# Revit family: VENTS-VKP_EC
name_source: partatom
category: Mechanical Equipment
units: mm (PartAtom-declared; Revit-internal decimal feet)

## family parameters
Always vertical = Yes
Classification = None
Cut with Voids When Loaded = No
OmniClass Number = 23.75.35.17.11
OmniClass Title = Fans for Air Ductwork
Part Type = Breaks Into
Room Calculation Point = No
Round Connector Dimension = Use Diameter
Shared = No
Work Plane-Based = No

## types (16) — shared parameters
Casing Material = Fan Zinc
Description = Inline centrifugal fan for rectangular ducts
Distribution Box Material = Distribution Box
Family Version = 1.0
Load Classification = HVAC
Maintenance Zone Height = 600 mm
Maintenance Zone Material = Maintenance Zone
Manufacturer = Vents
Motor Material = Painted Steel Black
Power Factor = 1
Protection rating = IP X4
Transported Air Temperature (°C) = -25...+40
URL = https://ventilation-system.com
dFl = 20 mm  [stored 0.0656168 ft]

## per-type parameters (varying)
- VKP 300x150 M1 EC: Apparent Power=97 VA; B=300 mm; B2=340 mm; Connection H=150 mm; Connection W=300 mm; Current=1 A; H=150 mm; H2=190 mm; L=350 mm; Maintenance Zone Length=350 mm; Maintenance Zone Width=300 mm; Maximum Air Flow=565 m³/h; Motor=No; Noise Level at 3 m (dBa)=44; Number of Poles=1; Power=97 W; RPM (min-1)=3300; Type Comments=Inline centrifugal fan VKP 300x150 M1 EC; Voltage=230 V; Weight=5.50 kg; eL=150 mm; eW=85 mm  [stored 0.278871 ft]; gsD=150 mm; mD=96 mm  [stored 0.314961 ft]; mH1=1 mm  [stored 0.00328084 ft]; mH2=30 mm  [stored 0.0984252 ft]; mL=145 mm  [stored 0.475722 ft]; mLW=122 mm  [stored 0.400262 ft]; mW=127 mm
- VKP 300х150 L1 EC: Apparent Power=101 VA; B=300 mm; B2=340 mm; Connection H=150 mm; Connection W=300 mm; Current=1 A; H=150 mm; H2=190 mm; L=350 mm; Maintenance Zone Length=350 mm; Maintenance Zone Width=300 mm; Maximum Air Flow=665 m³/h; Motor=Yes; Noise Level at 3 m (dBa)=46; Number of Poles=1; Power=101 W; RPM (min-1)=3500; Type Comments=Inline centrifugal fan VKP 300х150 L1 EC; Voltage=230 V; Weight=6.00 kg; eL=145 mm  [stored 0.475722 ft]; eW=68 mm; gsD=150 mm; mD=96 mm  [stored 0.314961 ft]; mH1=1 mm  [stored 0.00328084 ft]; mH2=30 mm  [stored 0.0984252 ft]; mL=145 mm  [stored 0.475722 ft]; mLW=122 mm  [stored 0.400262 ft]; mW=127 mm
- VKP 400x200 M1 EC: Apparent Power=91 VA; B=400 mm; B2=440 mm; Connection H=200 mm  [stored 0.656168 ft]; Connection W=400 mm; Current=1 A; H=200 mm  [stored 0.656168 ft]; H2=240 mm  [stored 0.787402 ft]; L=440 mm; Maintenance Zone Length=440 mm; Maintenance Zone Width=400 mm; Maximum Air Flow=810 m³/h; Motor=No; Noise Level at 3 m (dBa)=43; Number of Poles=1; Power=91 W; RPM (min-1)=2470; Type Comments=Inline centrifugal fan VKP 400x200 M1 EC; Voltage=230 V; Weight=8.30 kg; eL=195 mm  [stored 0.639764 ft]; eW=148 mm  [stored 0.485564 ft]; gsD=200 mm  [stored 0.656168 ft]; mD=96 mm  [stored 0.314961 ft]; mH1=1 mm  [stored 0.00328084 ft]; mH2=30 mm  [stored 0.0984252 ft]; mL=145 mm  [stored 0.475722 ft]; mLW=122 mm  [stored 0.400262 ft]; mW=127 mm
- VKP 400x200 L1 EC: Apparent Power=192 VA; B=400 mm; B2=440 mm; Connection H=200 mm  [stored 0.656168 ft]; Connection W=400 mm; Current=1 A; H=200 mm  [stored 0.656168 ft]; H2=240 mm  [stored 0.787402 ft]; L=440 mm; Maintenance Zone Length=440 mm; Maintenance Zone Width=400 mm; Maximum Air Flow=1190 m³/h; Motor=Yes; Noise Level at 3 m (dBa)=47; Number of Poles=1; Power=192 W; RPM (min-1)=3010; Type Comments=Inline centrifugal fan VKP 400x200 L1 EC; Voltage=230 V; Weight=10.00 kg; eL=195 mm  [stored 0.639764 ft]; eW=117 mm  [stored 0.383858 ft]; gsD=200 mm  [stored 0.656168 ft]; mD=114 mm  [stored 0.374016 ft]; mH1=1 mm  [stored 0.00328084 ft]; mH2=40 mm  [stored 0.131234 ft]; mL=195 mm  [stored 0.639764 ft]; mLW=142 mm  [stored 0.465879 ft]; mW=167 mm  [stored 0.5479 ft]
- VKP 500x250 M1 EC: Apparent Power=252 VA; B=500 mm; B2=540 mm; Connection H=250 mm  [stored 0.82021 ft]; Connection W=500 mm; Current=2 A; H=250 mm  [stored 0.82021 ft]; H2=290 mm; L=530 mm; Maintenance Zone Length=530 mm; Maintenance Zone Width=500 mm; Maximum Air Flow=1590 m³/h; Motor=Yes; Noise Level at 3 m (dBa)=45; Number of Poles=1; Power=252 W; RPM (min-1)=2500; Type Comments=Inline centrifugal fan VKP 500x250 M1 EC; Voltage=230 V; Weight=15.70 kg; eL=208 mm; eW=122 mm  [stored 0.400262 ft]; gsD=250 mm  [stored 0.82021 ft]; mD=114 mm  [stored 0.374016 ft]; mH1=1 mm  [stored 0.00328084 ft]; mH2=42 mm  [stored 0.137795 ft]; mL=215 mm; mLW=142 mm  [stored 0.465879 ft]; mW=208 mm
- VKP 500x250 L1 EC: Apparent Power=555 VA; B=500 mm; B2=540 mm; Connection H=250 mm  [stored 0.82021 ft]; Connection W=500 mm; Current=4 A; H=250 mm  [stored 0.82021 ft]; H2=290 mm; L=530 mm; Maintenance Zone Length=530 mm; Maintenance Zone Width=500 mm; Maximum Air Flow=2480 m³/h; Motor=Yes; Noise Level at 3 m (dBa)=51; Number of Poles=1; Power=555 W; RPM (min-1)=3100; Type Comments=Inline centrifugal fan VKP 500x250 L1 EC; Voltage=230 V; Weight=17.90 kg; eL=208 mm; eW=117 mm  [stored 0.383858 ft]; gsD=250 mm  [stored 0.82021 ft]; mD=153 mm  [stored 0.501969 ft]; mH1=42 mm  [stored 0.137795 ft]; mH2=47 mm  [stored 0.154199 ft]; mL=215 mm; mLW=192 mm  [stored 0.629921 ft]; mW=208 mm
- VKP 500x300 L1 EC: Apparent Power=445 VA; B=500 mm; B2=540 mm; Connection H=300 mm; Connection W=500 mm; Current=3 A; H=300 mm; H2=340 mm; L=530 mm; Maintenance Zone Length=530 mm; Maintenance Zone Width=500 mm; Maximum Air Flow=3230 m³/h; Motor=Yes; Noise Level at 3 m (dBa)=51; Number of Poles=1; Power=445 W; RPM (min-1)=3100; Type Comments=Inline centrifugal fan VKP 500x300 L1 EC; Voltage=230 V; Weight=18.70 kg; eL=208 mm; eW=117 mm  [stored 0.383858 ft]; gsD=250 mm  [stored 0.82021 ft]; mD=153 mm  [stored 0.501969 ft]; mH1=42 mm  [stored 0.137795 ft]; mH2=47 mm  [stored 0.154199 ft]; mL=215 mm; mLW=192 mm  [stored 0.629921 ft]; mW=208 mm
- VKP 600x300 M1 EC: Apparent Power=326 VA; B=600 mm; B2=640 mm; Connection H=300 mm; Connection W=600 mm; Current=2 A; H=300 mm; H2=340 mm; L=650 mm; Maintenance Zone Length=650 mm; Maintenance Zone Width=600 mm; Maximum Air Flow=2545 m³/h; Motor=Yes; Noise Level at 3 m (dBa)=48; Number of Poles=1; Power=326 W; RPM (min-1)=2000; Type Comments=Inline centrifugal fan VKP 600x300 M1 EC; Voltage=230 V; Weight=24.10 kg; eL=342 mm; eW=178 mm  [stored 0.58399 ft]; gsD=300 mm; mD=153 mm  [stored 0.501969 ft]; mH1=39 mm  [stored 0.127953 ft]; mH2=47 mm  [stored 0.154199 ft]; mL=265 mm; mLW=192 mm  [stored 0.629921 ft]; mW=252 mm
- VKP 600x350 M1 EC: Apparent Power=361 VA; B=600 mm; B2=640 mm; Connection H=350 mm; Connection W=600 mm; Current=3 A; H=350 mm; H2=390 mm; L=650 mm; Maintenance Zone Length=650 mm; Maintenance Zone Width=600 mm; Maximum Air Flow=2815 m³/h; Motor=Yes; Noise Level at 3 m (dBa)=49; Number of Poles=1; Power=361 W; RPM (min-1)=2000; Type Comments=Inline centrifugal fan VKP 600x350 M1 EC; Voltage=230 V; Weight=25.20 kg; eL=342 mm; eW=178 mm  [stored 0.58399 ft]; gsD=300 mm; mD=153 mm  [stored 0.501969 ft]; mH1=39 mm  [stored 0.127953 ft]; mH2=47 mm  [stored 0.154199 ft]; mL=265 mm; mLW=192 mm  [stored 0.629921 ft]; mW=252 mm
- VKP 600x350 LЗ EC: Apparent Power=1308 VA; B=600 mm; B2=640 mm; Connection H=350 mm; Connection W=600 mm; Current=2 A; H=350 mm; H2=390 mm; L=650 mm; Maintenance Zone Length=650 mm; Maintenance Zone Width=600 mm; Maximum Air Flow=4290 m³/h; Motor=Yes; Noise Level at 3 m (dBa)=55; Number of Poles=3; Power=1308 W; RPM (min-1)=3160; Type Comments=Inline centrifugal fan VKP 600x350 LЗ EC; Voltage=400 V; Weight=36.00 kg; eL=342 mm; eW=117 mm  [stored 0.383858 ft]; gsD=300 mm; mD=230 mm  [stored 0.754593 ft]; mH1=65 mm  [stored 0.213255 ft]; mH2=75 mm; mL=265 mm; mLW=288 mm; mW=252 mm
- VKP 700x400 M1 EC: Apparent Power=795 VA; B=700 mm; B2=740 mm; Connection H=400 mm; Connection W=700 mm; Current=3 A; H=400 mm; H2=440 mm; L=750 mm; Maintenance Zone Length=750 mm; Maintenance Zone Width=700 mm; Maximum Air Flow=5710 m³/h; Motor=Yes; Noise Level at 3 m (dBa)=53; Number of Poles=1; Power=795 W; RPM (min-1)=1400; Type Comments=Inline centrifugal fan VKP 700x400 M1 EC; Voltage=230 V; Weight=42.20 kg; eL=315 mm; eW=188 mm  [stored 0.616798 ft]; gsD=350 mm; mD=171 mm  [stored 0.561024 ft]; mH1=15 mm  [stored 0.0492126 ft]; mH2=60 mm  [stored 0.19685 ft]; mL=330 mm; mLW=288 mm; mW=292 mm
- VKP 700x400 LЗ EC: Apparent Power=2748 VA; B=700 mm; B2=740 mm; Connection H=400 mm; Connection W=700 mm; Current=3 A; H=400 mm; H2=440 mm; L=750 mm; Maintenance Zone Length=750 mm; Maintenance Zone Width=700 mm; Maximum Air Flow=6810 m³/h; Motor=Yes; Noise Level at 3 m (dBa)=57; Number of Poles=3; Power=2748 W; RPM (min-1)=2530; Type Comments=Inline centrifugal fan VKP 700x400 LЗ EC; Voltage=400 V; Weight=43.00 kg; eL=315 mm; eW=188 mm  [stored 0.616798 ft]; gsD=350 mm; mD=230 mm  [stored 0.754593 ft]; mH1=60 mm  [stored 0.19685 ft]; mH2=74 mm  [stored 0.242782 ft]; mL=330 mm; mLW=288 mm; mW=292 mm
- VKP 800x500 MЗ EC: Apparent Power=2025 VA; B=800 mm; B2=840 mm; Connection H=500 mm; Connection W=800 mm; Current=2 A; H=500 mm; H2=540 mm; L=850 mm; Maintenance Zone Length=850 mm; Maintenance Zone Width=800 mm; Maximum Air Flow=8395 m³/h; Motor=Yes; Noise Level at 3 m (dBa)=60; Number of Poles=3; Power=2025 W; RPM (min-1)=1470; Type Comments=Inline centrifugal fan VKP 800x500 MЗ EC; Voltage=400 V; Weight=62.30 kg; eL=352 mm; eW=248 mm  [stored 0.813648 ft]; gsD=400 mm; mD=229 mm; mH1=60 mm  [stored 0.19685 ft]; mH2=74 mm  [stored 0.242782 ft]; mL=365 mm; mLW=288 mm; mW=338 mm
- VKP 800x500 LЗ EC: Apparent Power=2925 VA; B=800 mm; B2=840 mm; Connection H=500 mm; Connection W=800 mm; Current=3 A; H=500 mm; H2=540 mm; L=850 mm; Maintenance Zone Length=850 mm; Maintenance Zone Width=800 mm; Maximum Air Flow=8535 m³/h; Motor=Yes; Noise Level at 3 m (dBa)=63; Number of Poles=3; Power=2925 W; RPM (min-1)=2400; Type Comments=Inline centrifugal fan VKP 800x500 LЗ EC; Voltage=400 V; Weight=54.30 kg; eL=352 mm; eW=248 mm  [stored 0.813648 ft]; gsD=400 mm; mD=229 mm; mH1=15 mm  [stored 0.0492126 ft]; mH2=78 mm  [stored 0.255906 ft]; mL=365 mm; mLW=288 mm; mW=338 mm
- VKP 900x500 LЗ EC: Apparent Power=3429 VA; B=900 mm; B2=940 mm; Connection H=500 mm; Connection W=900 mm; Current=5 A; H=500 mm; H2=540 mm; L=950 mm; Maintenance Zone Length=950 mm; Maintenance Zone Width=900 mm; Maximum Air Flow=11190 m³/h; Motor=Yes; Noise Level at 3 m (dBa)=66; Number of Poles=3; Power=3429 W; RPM (min-1)=1800; Type Comments=Inline centrifugal fan VKP 900x500 LЗ EC; Voltage=400 V; Weight=72.00 kg; eL=395 mm; eW=293 mm; gsD=450 mm; mD=229 mm; mH1=60 mm  [stored 0.19685 ft]; mH2=74 mm  [stored 0.242782 ft]; mL=405 mm; mLW=288 mm; mW=373 mm
- VKP 1000x500 LЗ EC: Apparent Power=2329 VA; B=1000 mm; B2=1040 mm; Connection H=500 mm; Connection W=1000 mm; Current=5 A; H=500 mm; H2=540 mm; L=950 mm; Maintenance Zone Length=950 mm; Maintenance Zone Width=1000 mm; Maximum Air Flow=11190 m³/h; Motor=Yes; Noise Level at 3 m (dBa)=66; Number of Poles=3; Power=2329 W; RPM (min-1)=1800; Type Comments=Inline centrifugal fan VKP 1000x500 LЗ EC; Voltage=400 V; Weight=77.00 kg; eL=405 mm; eW=343 mm; gsD=500 mm; mD=229 mm; mH1=60 mm  [stored 0.19685 ft]; mH2=74 mm  [stored 0.242782 ft]; mL=415 mm; mLW=288 mm; mW=423 mm

note: column(s) folded — value = type name in every type: Model

note: [stored X ft] marks values corroborated as IEEE doubles in the binary element streams (Revit-internal decimal feet)

## geometry (parser evidence)
native form markers: Sweep x11
no freeform markers — native parametric forms only
